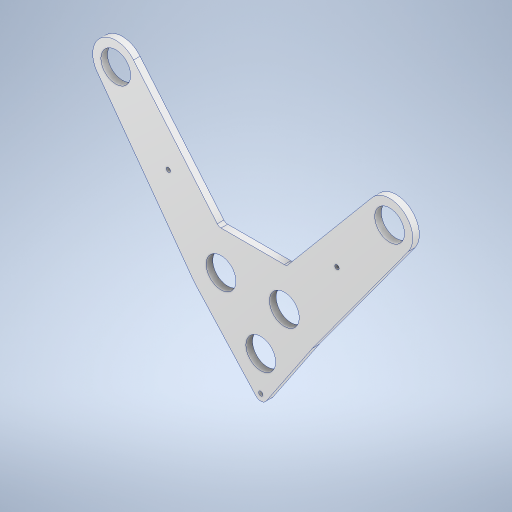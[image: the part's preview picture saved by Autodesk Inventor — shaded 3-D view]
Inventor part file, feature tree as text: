
AUTODESK INVENTOR PART (.ipt)
format: ipt  version: 2024 (Build 280153000, 153)  size: 318,976 bytes
history: native  units: in
note: dims shown in document units (in); Inventor stores cm internally (conversion verified against a paired STEP export)
features: thread x3, extrude x1, sketch x1
ambient origin geometry x8: Origin, YZ Plane, XZ Plane, XY Plane, X Axis, Y Axis, Z Axis, Center Point
bodies: Solid1 (feature_tree)
feature tree (5):
  extrude  "Extrusion1"  Depth=0.25in
  thread  "Thread1"  [1 undecoded]
  thread  "Thread2"  [1 undecoded]
  thread  "Thread3"  [1 undecoded]
  sketch  "Sketch1"  dims[d0=1.8in d1=2.4in d2=0.1in d3=0.1in d4=0.125in d5=1.125in d6=1.654in d7=1.504in d14=1.75in d15=1.75in d16=0.1875in d17=0.1667in d18=0.159in d19=0.159in d20=0.5in d21=0.5in d23=0.0625in d24=6.209in d25=4.0in d26=4.0in d27=0.25in d28=0.0in d29=0.25in d30=0.0in d31=0.25in d32=0.0in d33=0.25in d34=0.0in]
note: 3 required parameter values undecoded (feature->parameter linkage not recoverable at this tier; creation-order binding heuristic only, values carry confidence <= 0.55)
